# Revit family: CARE SUPPORT WELS 4 STAR SHOWER & INVERTED T GRAB RAIL 1.1M RH
name_source: partatom
category: Plumbing Fixtures
units: mm (PartAtom-declared; Revit-internal decimal feet)

## family parameters
Cut with Voids When Loaded = No
Host = Face
OmniClass Number = 23.45.05.14.17
OmniClass Title = Showers
Part Type = Normal
Room Calculation Point = No
Round Connector Dimension = Use Diameter
Shared = No

## types (3) — shared parameters
Assembly Code = D2010710
CW Connection = Yes
HW Connection = Yes
Manufacturer = GWA Bathrooms & Kitchens
URL = https://www.caroma.com.au
Vent Connection = No
Waste Connection = No
zero-valued in all types: Default Elevation

## per-type parameters (varying)
| type | Material | Material_Face | Material_Sprays | Model |
| CARE SUPPORT WELS 4 STAR SHOWER & INVERTED T GRAB RAIL 1.1M RH - CHROME | GWA_Metal-Chrome | GWA-Plastic-White | GWA-Plastic-General | 91125C4E |
| CARE SUPPORT WELS 4 STAR SHOWER & INVERTED T GRAB RAIL 1.1M RH - MATTE BLACK | GWA-Metal-Black | GWA-Plastic-Black | GWA-Plastic-Black | 91125B4E |
| CARE SUPPORT WELS 4 STAR SHOWER & INVERTED T GRAB RAIL 1.1M RH - BRUSHED NICKEL | GWA_Metal-Brushed-Nickel | GWA-Plastic-White | GWA-Plastic-General | 91125BN4E |

note: column(s) folded — value = type name in every type: Description

## geometry (parser evidence)
native form markers: Blend x4, Sweep x4
no freeform markers — native parametric forms only
